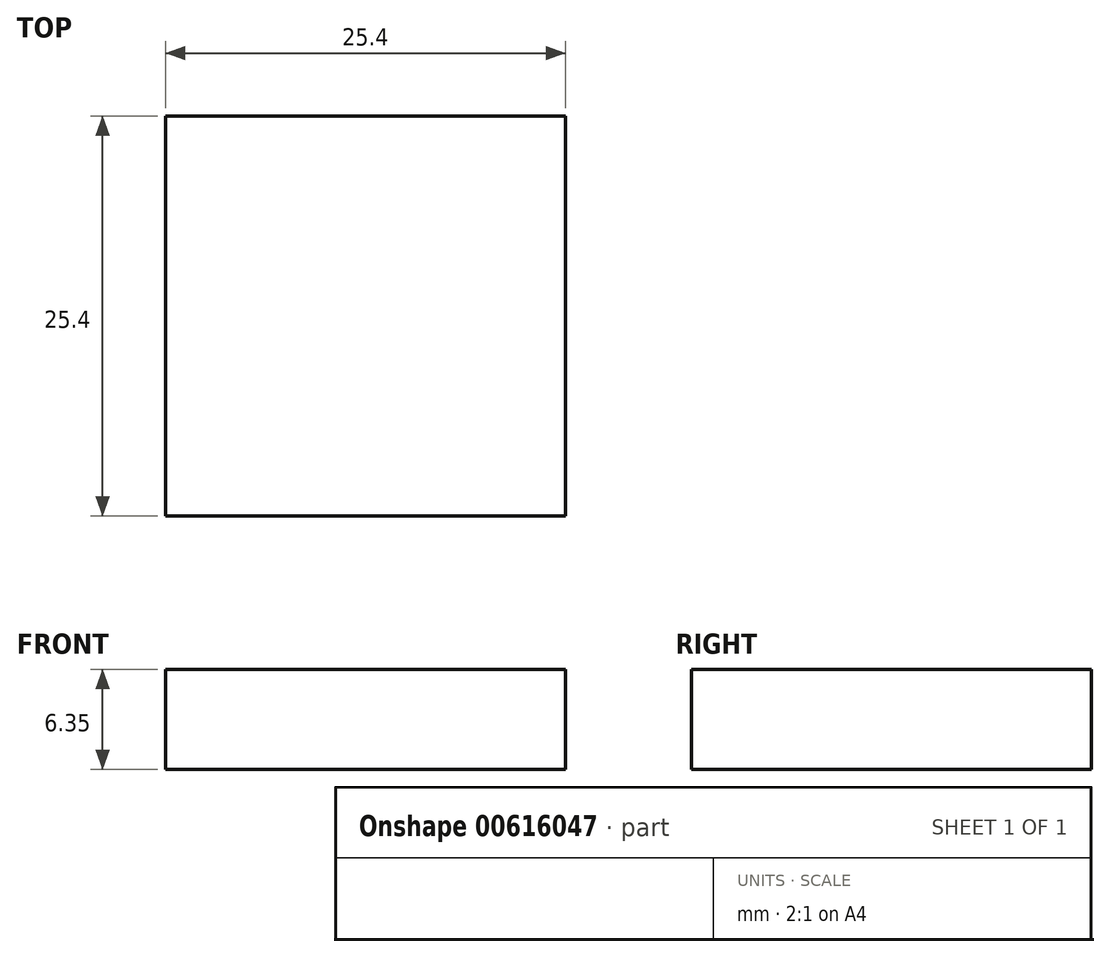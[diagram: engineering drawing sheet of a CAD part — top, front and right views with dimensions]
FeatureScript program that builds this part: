
annotation { "Feature Type Name" : "Feature", "Feature Type Description" : "" }
export const myFeature = defineFeature(function(context is Context, id is Id, definition is map)
    precondition{}
    {
        {
            var Q0;
            Q0=qCreatedBy(makeId("Top.planeOp"),FACE);
            var sketch = newSketch(context, id + "F0", { "sketchPlane" : qUnion([Q0])});
            skLineSegment(sketch, "E0.bottom", {"start": v(12.7, 12.7) * mm, "end": v(-12.7, 12.7) * mm});
            skLineSegment(sketch, "E0.top", {"start": v(12.7, -12.7) * mm, "end": v(-12.7, -12.7) * mm});
            skLineSegment(sketch, "E0.left", {"start": v(12.7, 12.7) * mm, "end": v(12.7, -12.7) * mm});
            skLineSegment(sketch, "E0.right", {"start": v(-12.7, 12.7) * mm, "end": v(-12.7, -12.7) * mm});
            skPoint(sketch, "E0.middle", {"position": v(0, 0) * mm});
            skSolve(sketch);
        }
        {
            var Q0;
            Q0=makeQuery(id+"F0.imprint","IMPRINT",FACE,{"disambiguationData":[TD([[makeQuery(id+"F0.imprint","IMPRINT",EDGE,{"derivedFrom":sQuery(id+"F0.wireOp",EDGE,"E0.bottom")}),1.0]])]});
            extrude(context, id + "F1", {"entities" : qUnion([Q0]), "depth" : 6.35 * mm, "offsetDistance" : 25.4 * mm});
        }
    });
